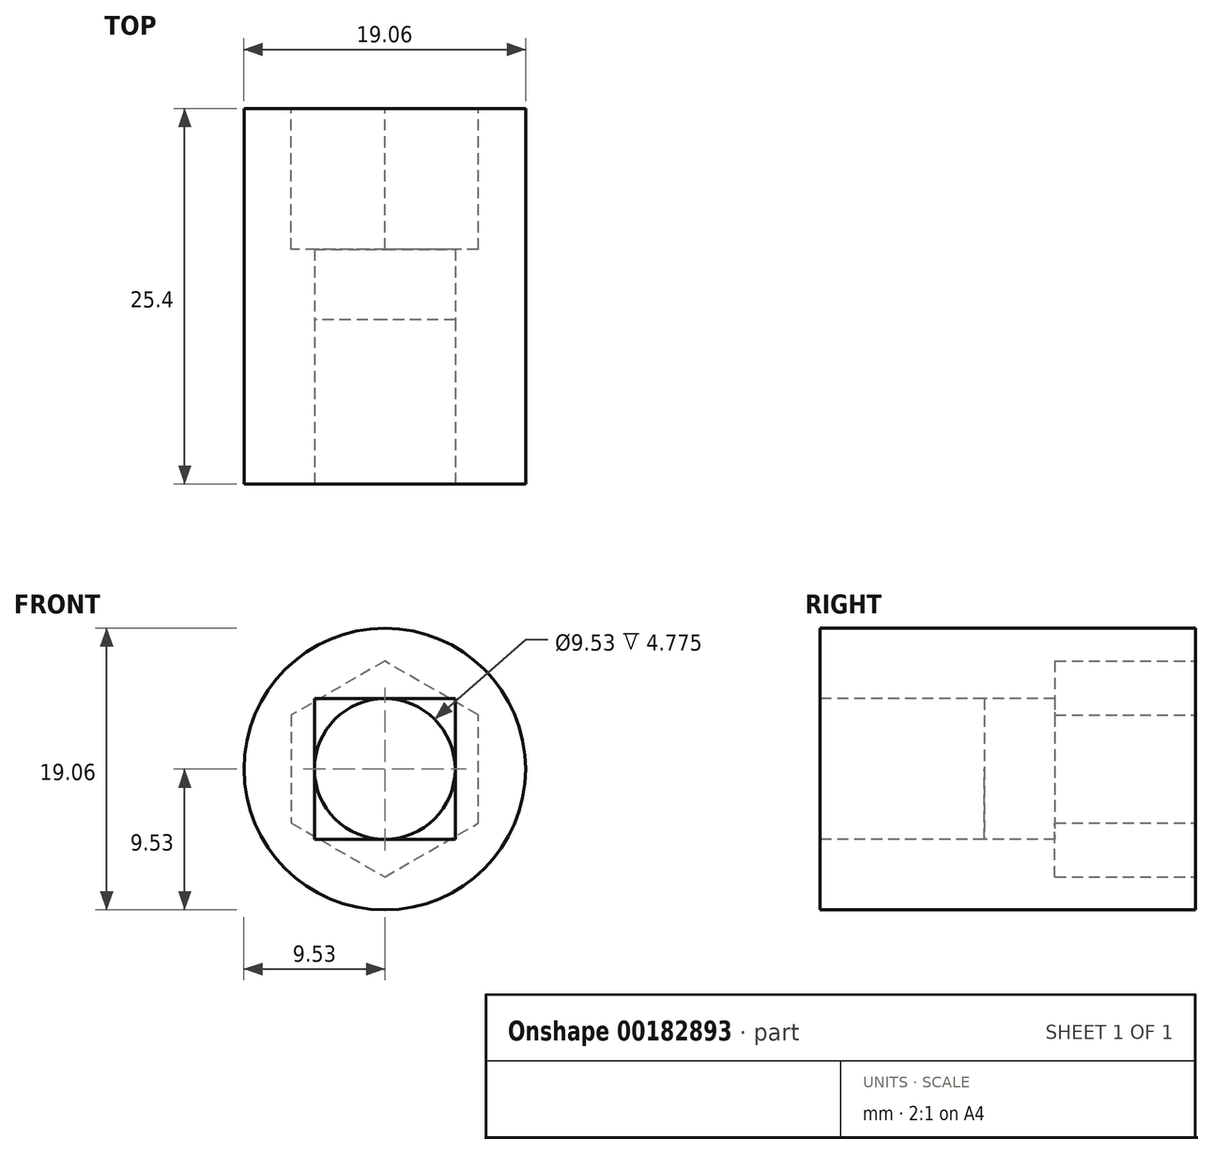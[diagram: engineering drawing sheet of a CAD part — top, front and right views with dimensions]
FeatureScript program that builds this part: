
annotation { "Feature Type Name" : "Feature", "Feature Type Description" : "" }
export const myFeature = defineFeature(function(context is Context, id is Id, definition is map)
    precondition{}
    {
        {
            var Q0;
            Q0=qCreatedBy(makeId("Front.planeOp"),FACE);
            var sketch = newSketch(context, id + "F0", { "sketchPlane" : qUnion([Q0])});
            skCircle(sketch, "E0", {"center": v(0, 0) * mm, "radius": 9.53 * mm});
            skSolve(sketch);
        }
        {
            var Q0;
            Q0=makeQuery(id+"F0.imprint","IMPRINT",FACE,{"disambiguationData":[TD([[makeQuery(id+"F0.imprint","IMPRINT",EDGE,{"derivedFrom":sQuery(id+"F0.wireOp",EDGE,"E0")}),1.0]])]});
            extrude(context, id + "F1", {"entities" : qUnion([Q0]), "depth" : 25.4 * mm});
        }
        {
            var Q0;
            Q0=makeQuery(id+"F1.opExtrude","CAP_FACE",FACE,{"disambiguationData":[OSD([sQuery(id+"F0.wireOp",EDGE,"E0")])],"isStart":false});
            var sketch = newSketch(context, id + "F2", { "sketchPlane" : qUnion([Q0])});
            skLineSegment(sketch, "E1.bottom", {"start": v(4.76, 4.76) * mm, "end": v(-4.76, 4.76) * mm});
            skLineSegment(sketch, "E1.top", {"start": v(4.76, -4.76) * mm, "end": v(-4.76, -4.76) * mm});
            skLineSegment(sketch, "E1.left", {"start": v(4.76, 4.76) * mm, "end": v(4.76, -4.76) * mm});
            skLineSegment(sketch, "E1.right", {"start": v(-4.76, 4.76) * mm, "end": v(-4.76, -4.76) * mm});
            skPoint(sketch, "E1.middle", {"position": v(0, 0) * mm});
            skCircle(sketch, "E2", {"center": v(0, 0) * mm, "radius": 4.76 * mm});
            skSolve(sketch);
        }
        {
            var Q0;
            {var subQ0=sQuery(id+"F2.wireOp",EDGE,"E2");var subQ1=makeQuery(id+"F2.imprint","INTERSECT",VERTEX,{"derivedFrom":[sQuery(id+"F2.wireOp",EDGE,"E1.bottom"),subQ0]});Q0=makeQuery(id+"F2.imprint","IMPRINT",FACE,{"disambiguationData":[TD([[makeQuery(id+"F2.imprint","IMPRINT",EDGE,{"disambiguationData":[TD([[subQ1,1.0]])],"derivedFrom":subQ0}),1.0]])]});}
            extrude(context, id + "F3", {"entities" : qUnion([Q0]), "operationType" : NewBodyOperationType.REMOVE, "endBound" : BoundingType.THROUGH_ALL, "oppositeDirection" : true, "depth" : 24.9 * mm});
        }
        {
            var Q0;
            Q0 = qSketchRegion(id + "F2", true);
            extrude(context, id + "F4", {"entities" : qUnion([Q0]), "operationType" : NewBodyOperationType.REMOVE, "oppositeDirection" : true, "depth" : 11.1 * mm});
        }
        {
            var Q0;
            Q0=makeQuery(id+"F1.opExtrude","CAP_FACE",FACE,{"disambiguationData":[OSD([sQuery(id+"F0.wireOp",EDGE,"E0")])],"isStart":true});
            var sketch = newSketch(context, id + "F5", { "sketchPlane" : qUnion([Q0])});
            skCircle(sketch, "E3.cCircle", {"center": v(0, 0) * mm, "radius": 6.32 * mm, "construction": true});
            skLineSegment(sketch, "E3.0", {"start": v(6.32, 3.65) * mm, "end": v(6.32, -3.65) * mm});
            skLineSegment(sketch, "E3.1", {"start": v(6.32, -3.65) * mm, "end": v(0, -7.3) * mm});
            skLineSegment(sketch, "E3.2", {"start": v(0, -7.3) * mm, "end": v(-6.32, -3.65) * mm});
            skLineSegment(sketch, "E3.3", {"start": v(-6.32, -3.65) * mm, "end": v(-6.32, 3.65) * mm});
            skLineSegment(sketch, "E3.4", {"start": v(-6.32, 3.65) * mm, "end": v(0, 7.3) * mm});
            skLineSegment(sketch, "E3.5", {"start": v(0, 7.3) * mm, "end": v(6.32, 3.65) * mm});
            skPoint(sketch, "E3.0.midPoint", {"position": v(6.32, 0) * mm});
            skSolve(sketch);
        }
        {
            var Q0;
            Q0 = qSketchRegion(id + "F5", true);
            extrude(context, id + "F6", {"entities" : qUnion([Q0]), "operationType" : NewBodyOperationType.REMOVE, "oppositeDirection" : true, "depth" : 9.52 * mm});
        }
    });
